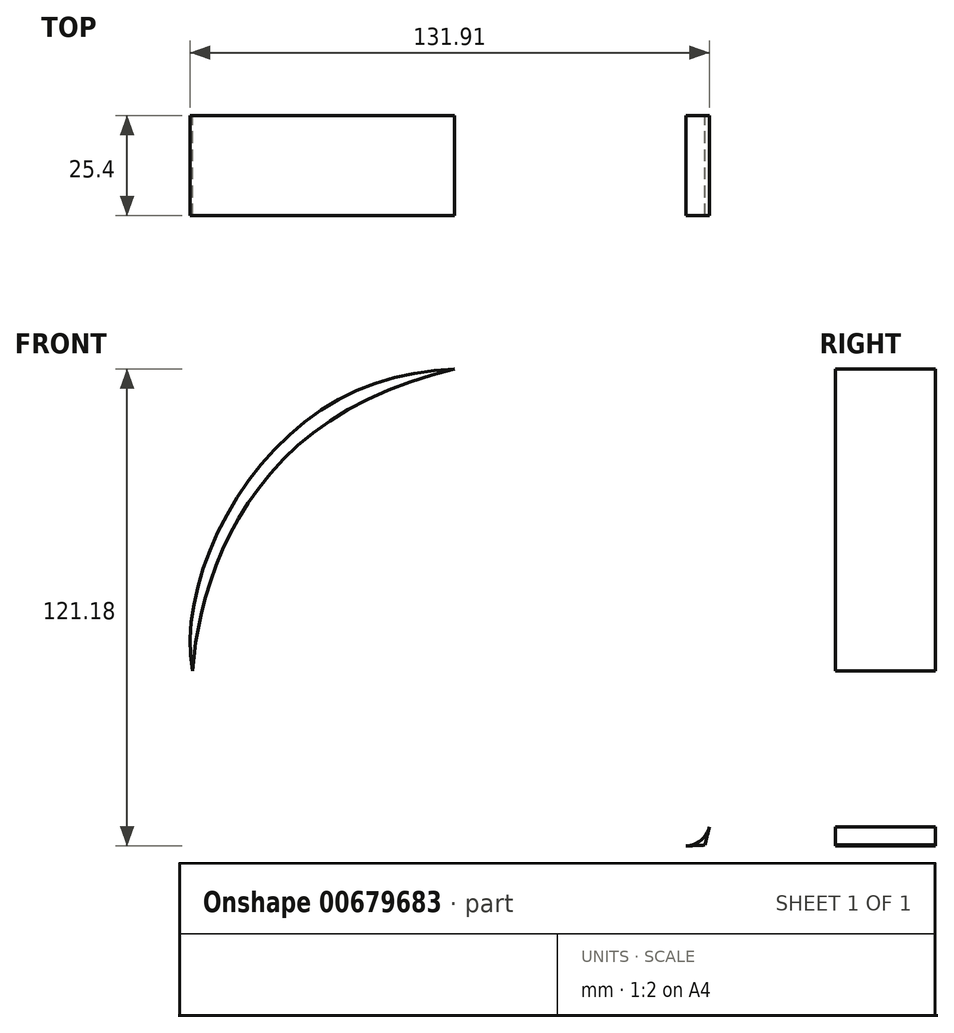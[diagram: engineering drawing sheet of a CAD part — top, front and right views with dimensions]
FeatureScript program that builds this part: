
annotation { "Feature Type Name" : "Feature", "Feature Type Description" : "" }
export const myFeature = defineFeature(function(context is Context, id is Id, definition is map)
    precondition{}
    {
        {
            var Q0;
            Q0=qCreatedBy(makeId("Front.planeOp"),FACE);
            var sketch = newSketch(context, id + "F0", { "sketchPlane" : qUnion([Q0])});
            skFitSpline(sketch, "E0", {"points": [v(57.19, 33.05) * mm, v(62.74, -68.55) * mm], "startDerivative": vector(83.99, -90.46) * mm, "endDerivative": vector(-15.43, -70.87) * mm});
            skFitSpline(sketch, "E1", {"points": [v(62.74, -68.55) * mm, v(-67.5, -24.26) * mm], "startDerivative": vector(-284.98, -14.8) * mm, "endDerivative": vector(-29.4, 89.64) * mm});
            skFitSpline(sketch, "E2", {"points": [v(-67.5, -24.26) * mm, v(-29.16, 45.33) * mm, v(57.19, 33.05) * mm], "startDerivative": vector(-24.45, 135.77) * mm, "endDerivative": vector(121.69, -106) * mm});
            skArc(sketch, "E3.filletArc", {"start": v(57.92, -68.78) * mm, "mid": v(61.67, -67.34) * mm, "end": v(63.81, -63.93) * mm});
            skFitSpline(sketch, "E4", {"points": [v(57.19, 33.05) * mm, v(-29.16, 41.38) * mm, v(-67.5, -24.26) * mm], "startDerivative": vector(-30.53, 171.84) * mm, "endDerivative": vector(-10.08, -126.35) * mm});
            skLineSegment(sketch, "E5", {"start": v(-67.5, -24.26) * mm, "end": v(57.19, 33.05) * mm});
            skSolve(sketch);
        }
        {
            var Q0;
            Q0=makeQuery(id+"F0.imprint","IMPRINT",FACE,{"disambiguationData":[TD([[makeQuery(id+"F0.imprint","IMPRINT",EDGE,{"derivedFrom":sQuery(id+"F0.wireOp",EDGE,"E0")}),-1.0]])]});
            var Q1;
            {var subQ0=sQuery(id+"F0.wireOp",EDGE,"E2");Q1=makeQuery(id+"F0.imprint","IMPRINT",FACE,{"disambiguationData":[TD([[makeQuery(id+"F0.imprint","IMPRINT",EDGE,{"derivedFrom":subQ0}),-1.0]])]});}
            extrude(context, id + "F1", {"entities" : qUnion([Q0, Q1]), "endBound" : BoundingType.SYMMETRIC, "depth" : 25.4 * mm, "offsetDistance" : 25.4 * mm});
        }
    });
